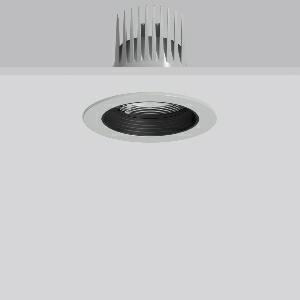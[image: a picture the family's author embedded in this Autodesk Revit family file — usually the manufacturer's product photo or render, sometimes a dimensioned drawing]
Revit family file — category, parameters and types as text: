
# Revit family: heledon_maxi_e_901760_004_2_76_3df5
name_source: partatom
category: Lighting Fixtures
units: mm (PartAtom-declared; Revit-internal decimal feet)

## family parameters
Cut with Voids When Loaded = No
Host = Face
Light Source = No
Part Type = Normal
Room Calculation Point = No
Round Connector Dimension = Use Diameter
Shared = No

## types (1)
- HELEDON maxi E (1 x LED Modul 927, 2650 lm, 2700)
    Apparent Load = 25 VA
    Approval mark = CE
    CIE Flux Codes = 97 100 100 100 100
    Color Rendering = 92
    Color Temperature = 2700
    Default Elevation = 1800 mm
    Description = Series: HELEDON maxi
Round recessed downlight. Housing: die-cast aluminium, powder-coated. Black plastic ring and recessed LED to prevent glare from the side. Optical assembly with lens made of plastic (polycarbonate) for the best homogeneous light distribution - can be changed without tools. Best colour rendering index Ra>90. Suitable for Recessed ceiling mounting. Installation without tools thanks to spring fastening system. Including separate LED converter with connecting cable 600 mm.High quality converter without flickering and stroboscopic effect. Through-wiring box (5 pole) available as accessory. The following accessories can be mounted without use of tools: interchangeable lenses, decorative glasses, honeycomb louvre, clear and frosted diffusers, white interchangeable plastic ring. 
Colour: silver
Diameter: 162 mm
Height: 3 mm
Cut-out diameter: 152 mm
Recess height: 200 mm
Luminaire: recess height: 135 mm
Lamp: LED
Socket: without socket
Colour temperature: 2700K
Colour rendering index (CRI): 92
System power: 25 W
Rated luminous flux: 2650 lm
Luminous efficiency: 106 lm/W
Control gear: Converter, dimmable, DALI
Protection class: II
Type of protection: IP 20
    Height = 0 mm  [stored 0 ft]
    Lamp = 1 x LED Modul 927
    Lamp Light Flux = 2650 lm
    Lamp count = 1
    Length = 162 mm
    Lifetime = 50000 h
    Luminous efficacy = 106 lm/W
    Manufacturer = RZB
    ModVariant = No
    Model = 901760.004.2.76
    Mounting Place = Ceiling
    Mounting Type = Recessed
    Number of Poles = 1
    OnlyDefault = Yes
    Power Factor = 1
    Product Name = HELEDON maxi E
    Product group = Recessed downlights
    ProductGroupID = 402
    Protection Class = Protection class II
    Protection Degree = IP 20
    RLX_Detail_Level = 1
    RLX_Emergency_Light_Flux = 0 lm
    RLX_Emergency_Type = 0
    RLX_Emergency_Type_DB = No
    RlxData = <blob elided: 119553 chars, md5=ca7b7596>
    Socket = socket
    Standby Power = 0 W
    System Light Flux = 2650 lm
    System Power = 25 W
    Type Comments = Product without accessories
    Type Image = 901663.004.jpg
    URL = http://relux.com
    VarID = ---
    Voltage = 230 V
    Voltage Range = 220-240 V
    Weight = 0.00 kg
    Width = 0 mm  [stored 0 ft]

note: [stored X ft] marks values corroborated as IEEE doubles in the binary element streams (Revit-internal decimal feet)

## geometry (parser evidence)
native form markers: Blend x4, Sweep x12
no freeform markers — native parametric forms only
